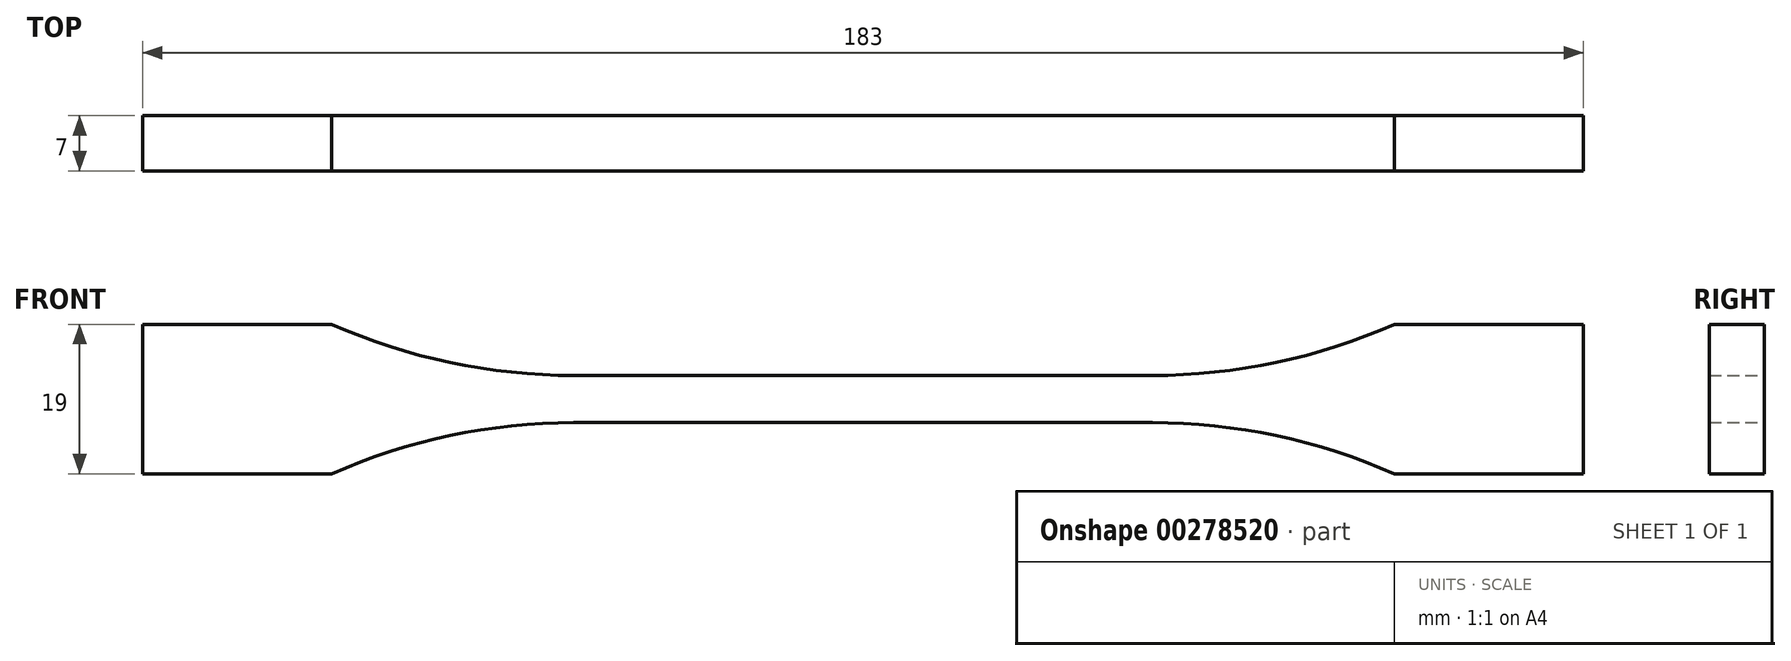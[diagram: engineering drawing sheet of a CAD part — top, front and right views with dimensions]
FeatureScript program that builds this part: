
annotation { "Feature Type Name" : "Feature", "Feature Type Description" : "" }
export const myFeature = defineFeature(function(context is Context, id is Id, definition is map)
    precondition{}
    {
        {
            var Q0;
            Q0=qCreatedBy(makeId("Front.planeOp"),FACE);
            var sketch = newSketch(context, id + "F0", { "sketchPlane" : qUnion([Q0])});
            skLineSegment(sketch, "E0", {"start": v(0, 3) * mm, "end": v(36.75, 3) * mm});
            skArc(sketch, "E1", {"start": v(36.75, 3) * mm, "mid": v(52.46, 4.64) * mm, "end": v(67.5, 9.5) * mm});
            skLineSegment(sketch, "E2", {"start": v(67.5, 9.5) * mm, "end": v(91.5, 9.5) * mm});
            skLineSegment(sketch, "E3.MirrorCS", {"start": v(67.5, -9.5) * mm, "end": v(91.5, -9.5) * mm});
            skLineSegment(sketch, "E4.MirrorCS", {"start": v(0, -3) * mm, "end": v(36.75, -3) * mm});
            skArc(sketch, "E5.MirrorCS", {"start": v(36.75, -3) * mm, "mid": v(52.46, -4.64) * mm, "end": v(67.5, -9.5) * mm});
            skLineSegment(sketch, "E6.MirrorCS", {"start": v(0, 3) * mm, "end": v(-36.75, 3) * mm});
            skArc(sketch, "E7.MirrorCS", {"start": v(-36.75, 3) * mm, "mid": v(-52.46, 4.64) * mm, "end": v(-67.5, 9.5) * mm});
            skLineSegment(sketch, "E8.MirrorCS", {"start": v(-67.5, 9.5) * mm, "end": v(-91.5, 9.5) * mm});
            skLineSegment(sketch, "E9.MirrorCS", {"start": v(-67.5, -9.5) * mm, "end": v(-91.5, -9.5) * mm});
            skArc(sketch, "E10.MirrorCS", {"start": v(-36.75, -3) * mm, "mid": v(-52.46, -4.64) * mm, "end": v(-67.5, -9.5) * mm});
            skLineSegment(sketch, "E11.MirrorCS", {"start": v(0, -3) * mm, "end": v(-36.75, -3) * mm});
            skLineSegment(sketch, "E12", {"start": v(-91.5, 9.5) * mm, "end": v(-91.5, -9.5) * mm});
            skLineSegment(sketch, "E13", {"start": v(91.5, 9.5) * mm, "end": v(91.5, -9.5) * mm});
            skSolve(sketch);
        }
        {
            var Q0;
            Q0=makeQuery(id+"F0.imprint","IMPRINT",FACE,{"disambiguationData":[TD([[makeQuery(id+"F0.imprint","IMPRINT",EDGE,{"derivedFrom":sQuery(id+"F0.wireOp",EDGE,"E1")}),-1.0]])]});
            extrude(context, id + "F1", {"entities" : qUnion([Q0]), "endBound" : BoundingType.SYMMETRIC, "depth" : 7 * mm});
        }
    });
